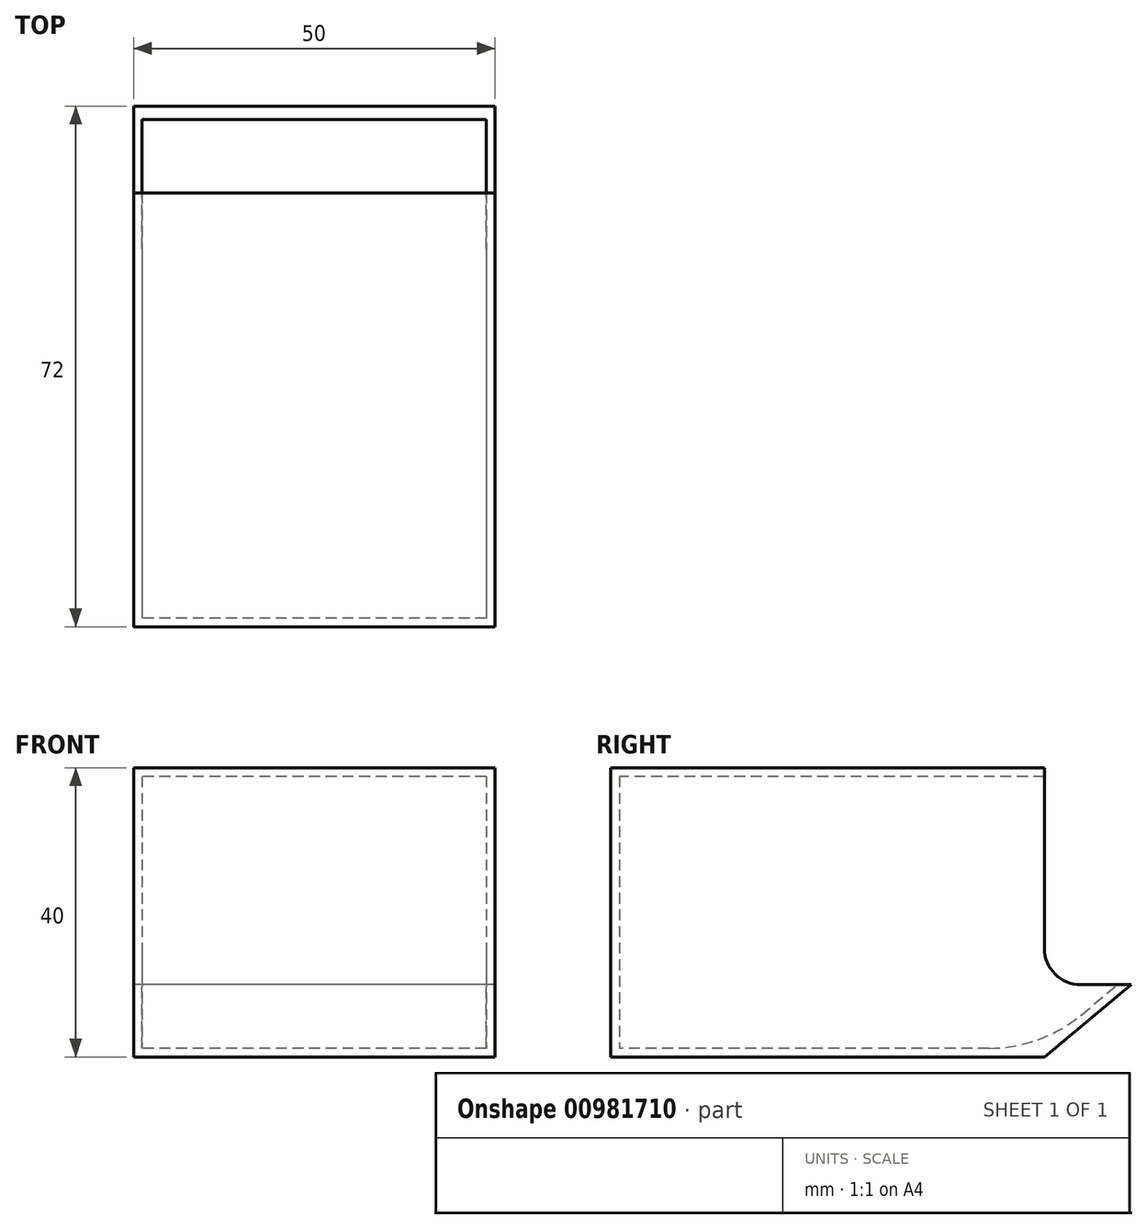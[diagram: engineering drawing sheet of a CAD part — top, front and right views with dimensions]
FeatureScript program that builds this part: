
annotation { "Feature Type Name" : "Feature", "Feature Type Description" : "" }
export const myFeature = defineFeature(function(context is Context, id is Id, definition is map)
    precondition{}
    {
        {
            var Q0;
            Q0=qCreatedBy(makeId("Right.planeOp"),FACE);
            var sketch = newSketch(context, id + "F0", { "sketchPlane" : qUnion([Q0])});
            skLineSegment(sketch, "E0.bottom", {"start": v(30, 20) * mm, "end": v(-30, 20) * mm});
            skLineSegment(sketch, "E0.top", {"start": v(30, -20) * mm, "end": v(-30, -20) * mm});
            skLineSegment(sketch, "E0.left", {"start": v(30, 20) * mm, "end": v(30, -20) * mm});
            skLineSegment(sketch, "E0.right", {"start": v(-30, 20) * mm, "end": v(-30, -20) * mm});
            skPoint(sketch, "E0.middle", {"position": v(0, 0) * mm});
            skLineSegment(sketch, "E1", {"start": v(30, -20) * mm, "end": v(42, -10) * mm});
            skLineSegment(sketch, "E2", {"start": v(42, -10) * mm, "end": v(30, -10) * mm});
            skSolve(sketch);
        }
        {
            var Q0;
            {var subQ3=sQuery(id+"F0.wireOp",EDGE,"E0.bottom");Q0=makeQuery(id+"F0.imprint","IMPRINT",FACE,{"disambiguationData":[TD([[makeQuery(id+"F0.imprint","IMPRINT",EDGE,{"derivedFrom":subQ3}),1.0]])]});}
            var Q1;
            {var subQ0=sQuery(id+"F0.wireOp",EDGE,"E1");Q1=makeQuery(id+"F0.imprint","IMPRINT",FACE,{"disambiguationData":[TD([[makeQuery(id+"F0.imprint","IMPRINT",EDGE,{"derivedFrom":subQ0}),1.0]])]});}
            extrude(context, id + "F1", {"entities" : qUnion([Q0, Q1]), "endBound" : BoundingType.SYMMETRIC, "depth" : 50 * mm, "offsetDistance" : 25 * mm});
        }
        {
            var Q0;
            Q0=makeQuery(id+"F1.opExtrude","SWEPT_FACE",FACE,{"disambiguationData":[OSD([sQuery(id+"F0.wireOp",EDGE,"E0.left")])]});
            var Q1;
            Q1=makeQuery(id+"F1.opExtrude","SWEPT_FACE",FACE,{"disambiguationData":[OSD([sQuery(id+"F0.wireOp",EDGE,"E2")])]});
            shell(context, id + "F2", {"entities" : qUnion([Q0, Q1]), "thickness" : 1.2 * mm});
        }
        {
            var Q0;
            Q0=makeQuery(id+"F2.opShell","OFFSET_EDGE",EDGE,{"disambiguationData":[OSD([sQuery(id+"F0.wireOp",EDGE,"E0.top"),sQuery(id+"F0.wireOp",EDGE,"E0.left"),sQuery(id+"F0.wireOp",EDGE,"E1")])]});
            fillet(context, id + "F3", {"entities" : qUnion([Q0]), "radius" : 20 * mm, "tangentPropagation" : true, "allowEdgeOverflow" : false});
        }
        {
            var Q0;
            Q0=makeQuery(id+"F1.opExtrude","SWEPT_EDGE",EDGE,{"disambiguationData":[OSD([sQuery(id+"F0.wireOp",EDGE,"E0.left"),sQuery(id+"F0.wireOp",EDGE,"E2")])]});
            var Q1;
            Q1=makeQuery(id+"F2.opShell","OFFSET_EDGE",EDGE,{"disambiguationData":[OSD([sQuery(id+"F0.wireOp",EDGE,"E0.left"),sQuery(id+"F0.wireOp",EDGE,"E2")])]});
            fillet(context, id + "F4", {"entities" : qUnion([Q0, Q1]), "radius" : 5 * mm, "tangentPropagation" : true, "allowEdgeOverflow" : false});
        }
    });
